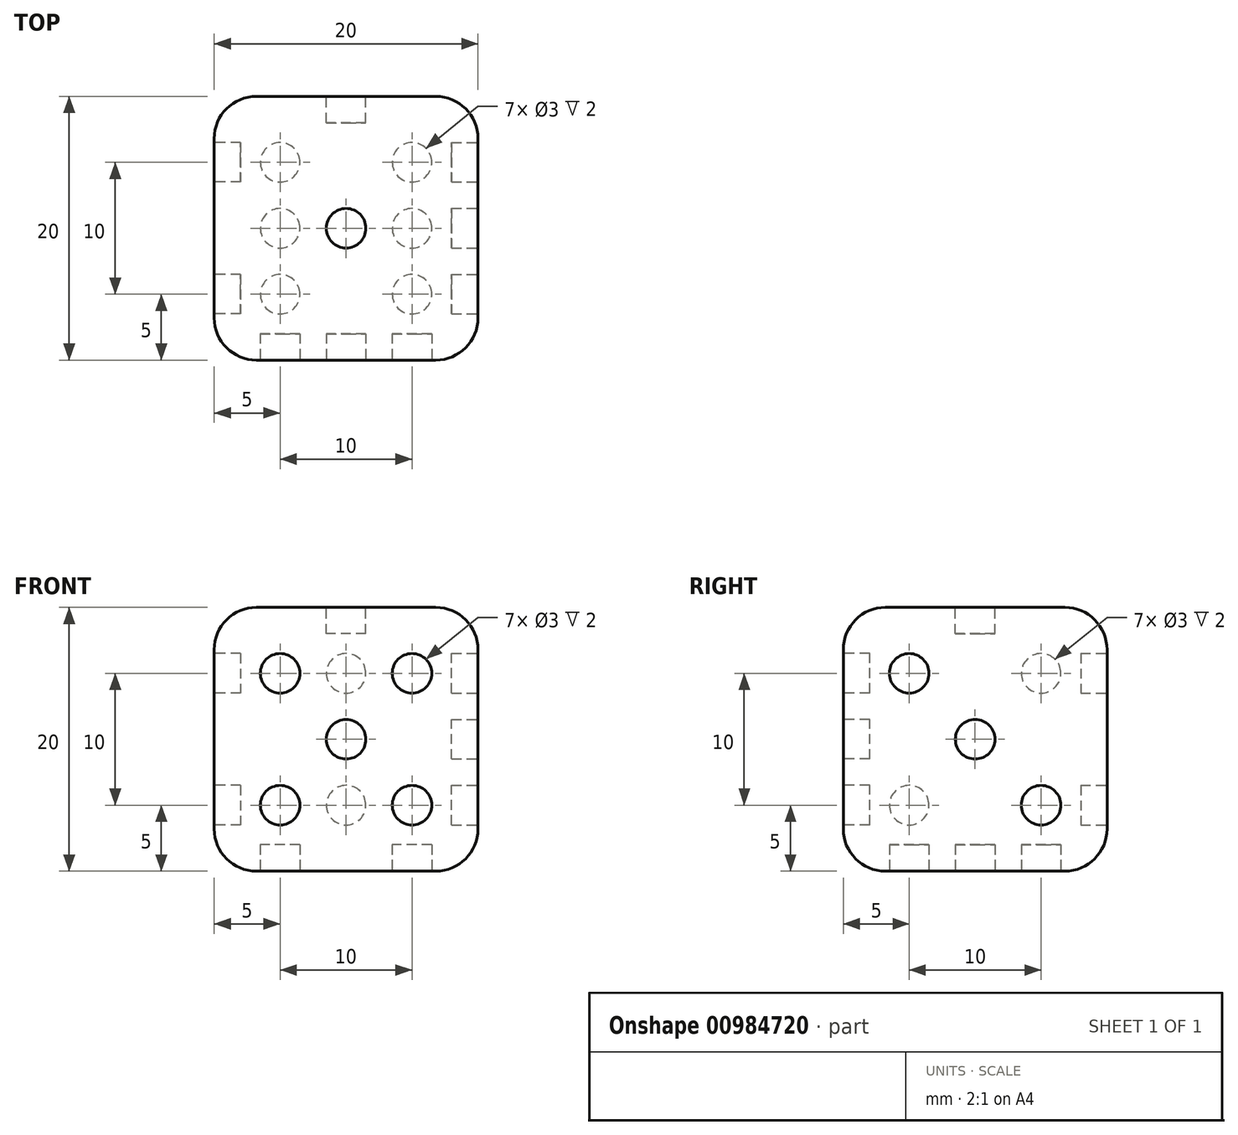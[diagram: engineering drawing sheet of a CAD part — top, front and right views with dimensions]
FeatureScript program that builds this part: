
annotation { "Feature Type Name" : "Feature", "Feature Type Description" : "" }
export const myFeature = defineFeature(function(context is Context, id is Id, definition is map)
    precondition{}
    {
        {
            var Q0;
            Q0=qCreatedBy(makeId("Top.planeOp"),FACE);
            var sketch = newSketch(context, id + "F0", { "sketchPlane" : qUnion([Q0])});
            skLineSegment(sketch, "E0.bottom", {"start": v(-10, -10) * mm, "end": v(10, -10) * mm});
            skLineSegment(sketch, "E0.top", {"start": v(-10, 10) * mm, "end": v(10, 10) * mm});
            skLineSegment(sketch, "E0.left", {"start": v(-10, -10) * mm, "end": v(-10, 10) * mm});
            skLineSegment(sketch, "E0.right", {"start": v(10, -10) * mm, "end": v(10, 10) * mm});
            skSolve(sketch);
        }
        {
            var Q0;
            Q0 = qSketchRegion(id + "F0", true);
            extrude(context, id + "F1", {"entities" : qUnion([Q0]), "depth" : 20 * mm, "offsetDistance" : 25 * mm});
        }
        {
            var Q0;
            Q0=makeQuery(id+"F0.imprint","IMPRINT",FACE,{"disambiguationData":[TD([[makeQuery(id+"F0.imprint","IMPRINT",EDGE,{"derivedFrom":sQuery(id+"F0.wireOp",EDGE,"E0.bottom")}),1.0]])]});
            var sketch = newSketch(context, id + "F2", { "sketchPlane" : qUnion([Q0])});
            skCircle(sketch, "E1", {"center": v(-5, 5) * mm, "radius": 1.5 * mm});
            skCircle(sketch, "E2.1.0.0", {"center": v(5, 5) * mm, "radius": 1.5 * mm});
            skLineSegment(sketch, "E2.direction1", {"start": v(-5, 5) * mm, "end": v(5, 5) * mm, "construction": true});
            skCircle(sketch, "E3.1.0.0", {"center": v(-5, 0) * mm, "radius": 1.5 * mm});
            skCircle(sketch, "E3.1.0.1", {"center": v(5, 0) * mm, "radius": 1.5 * mm});
            skCircle(sketch, "E3.2.0.0", {"center": v(-5, -5) * mm, "radius": 1.5 * mm});
            skCircle(sketch, "E3.2.0.1", {"center": v(5, -5) * mm, "radius": 1.5 * mm});
            skLineSegment(sketch, "E3.direction1", {"start": v(-5, 5) * mm, "end": v(-5, 0) * mm, "construction": true});
            skSolve(sketch);
        }
        {
            var Q0;
            Q0 = qSketchRegion(id + "F2", true);
            extrude(context, id + "F3", {"entities" : qUnion([Q0]), "operationType" : NewBodyOperationType.REMOVE, "depth" : 2 * mm, "offsetDistance" : 25 * mm});
        }
        {
            var Q0;
            Q0=makeQuery(id+"F1.opExtrude","CAP_FACE",FACE,{"disambiguationData":[OSD([sQuery(id+"F0.wireOp",EDGE,"E0.bottom"),sQuery(id+"F0.wireOp",EDGE,"E0.top"),sQuery(id+"F0.wireOp",EDGE,"E0.left"),sQuery(id+"F0.wireOp",EDGE,"E0.right")])],"isStart":false});
            var sketch = newSketch(context, id + "F4", { "sketchPlane" : qUnion([Q0])});
            skCircle(sketch, "E4", {"center": v(0, 0) * mm, "radius": 1.5 * mm});
            skSolve(sketch);
        }
        {
            var Q0;
            Q0 = qSketchRegion(id + "F4", true);
            extrude(context, id + "F5", {"entities" : qUnion([Q0]), "operationType" : NewBodyOperationType.REMOVE, "oppositeDirection" : true, "depth" : 2 * mm, "offsetDistance" : 25 * mm});
        }
        {
            var Q0;
            Q0=makeQuery(id+"F1.opExtrude","SWEPT_FACE",FACE,{"disambiguationData":[OSD([sQuery(id+"F0.wireOp",EDGE,"E0.bottom")])]});
            var sketch = newSketch(context, id + "F6", { "sketchPlane" : qUnion([Q0])});
            skCircle(sketch, "E5", {"center": v(0, 10) * mm, "radius": 1.5 * mm});
            skCircle(sketch, "E6", {"center": v(-5, 5) * mm, "radius": 1.5 * mm});
            skCircle(sketch, "E7.0.1.0", {"center": v(-5, 15) * mm, "radius": 1.5 * mm});
            skCircle(sketch, "E7.1.0.0", {"center": v(5, 5) * mm, "radius": 1.5 * mm});
            skCircle(sketch, "E7.1.1.0", {"center": v(5, 15) * mm, "radius": 1.5 * mm});
            skLineSegment(sketch, "E7.direction1", {"start": v(-5, 5) * mm, "end": v(5, 5) * mm, "construction": true});
            skLineSegment(sketch, "E7.direction2", {"start": v(-5, 5) * mm, "end": v(-5, 15) * mm, "construction": true});
            skSolve(sketch);
        }
        {
            var Q0;
            Q0 = qSketchRegion(id + "F6", true);
            extrude(context, id + "F7", {"entities" : qUnion([Q0]), "operationType" : NewBodyOperationType.REMOVE, "oppositeDirection" : true, "depth" : 2 * mm, "offsetDistance" : 25 * mm});
        }
        {
            var Q0;
            Q0=makeQuery(id+"F1.opExtrude","SWEPT_FACE",FACE,{"disambiguationData":[OSD([sQuery(id+"F0.wireOp",EDGE,"E0.left")])]});
            var sketch = newSketch(context, id + "F8", { "sketchPlane" : qUnion([Q0])});
            skCircle(sketch, "E8", {"center": v(-5, 5) * mm, "radius": 1.5 * mm});
            skCircle(sketch, "E9.0.1.0", {"center": v(-5, 15) * mm, "radius": 1.5 * mm});
            skCircle(sketch, "E9.1.0.0", {"center": v(5, 5) * mm, "radius": 1.5 * mm});
            skCircle(sketch, "E9.1.1.0", {"center": v(5, 15) * mm, "radius": 1.5 * mm});
            skLineSegment(sketch, "E9.direction1", {"start": v(-5, 5) * mm, "end": v(5, 5) * mm, "construction": true});
            skLineSegment(sketch, "E9.direction2", {"start": v(-5, 5) * mm, "end": v(-5, 15) * mm, "construction": true});
            skSolve(sketch);
        }
        {
            var Q0;
            Q0 = qSketchRegion(id + "F8", true);
            extrude(context, id + "F9", {"entities" : qUnion([Q0]), "operationType" : NewBodyOperationType.REMOVE, "oppositeDirection" : true, "depth" : 2 * mm, "offsetDistance" : 25 * mm});
        }
        {
            var Q0;
            Q0=makeQuery(id+"F1.opExtrude","SWEPT_FACE",FACE,{"disambiguationData":[OSD([sQuery(id+"F0.wireOp",EDGE,"E0.right")])]});
            var sketch = newSketch(context, id + "F10", { "sketchPlane" : qUnion([Q0])});
            skCircle(sketch, "E10", {"center": v(-5, 15) * mm, "radius": 1.5 * mm});
            skCircle(sketch, "E11", {"center": v(0, 10) * mm, "radius": 1.5 * mm});
            skCircle(sketch, "E12", {"center": v(5, 5) * mm, "radius": 1.5 * mm});
            skSolve(sketch);
        }
        {
            var Q0;
            Q0=makeQuery(id+"F10.imprint","IMPRINT",FACE,{"disambiguationData":[TD([[makeQuery(id+"F10.imprint","IMPRINT",EDGE,{"derivedFrom":sQuery(id+"F10.wireOp",EDGE,"E12")}),1.0]])]});
            var Q1;
            Q1=makeQuery(id+"F10.imprint","IMPRINT",FACE,{"disambiguationData":[TD([[makeQuery(id+"F10.imprint","IMPRINT",EDGE,{"derivedFrom":sQuery(id+"F10.wireOp",EDGE,"E11")}),1.0]])]});
            var Q2;
            Q2=makeQuery(id+"F10.imprint","IMPRINT",FACE,{"disambiguationData":[TD([[makeQuery(id+"F10.imprint","IMPRINT",EDGE,{"derivedFrom":sQuery(id+"F10.wireOp",EDGE,"E10")}),1.0]])]});
            extrude(context, id + "F11", {"entities" : qUnion([Q0, Q1, Q2]), "operationType" : NewBodyOperationType.REMOVE, "oppositeDirection" : true, "depth" : 2 * mm, "offsetDistance" : 25 * mm});
        }
        {
            var Q0;
            Q0=makeQuery(id+"F1.opExtrude","SWEPT_FACE",FACE,{"disambiguationData":[OSD([sQuery(id+"F0.wireOp",EDGE,"E0.top")])]});
            var sketch = newSketch(context, id + "F12", { "sketchPlane" : qUnion([Q0])});
            skCircle(sketch, "E13", {"center": v(0, 5) * mm, "radius": 1.5 * mm});
            skCircle(sketch, "E14", {"center": v(0, 15) * mm, "radius": 1.5 * mm});
            skSolve(sketch);
        }
        {
            var Q0;
            Q0=makeQuery(id+"F12.imprint","IMPRINT",FACE,{"disambiguationData":[TD([[makeQuery(id+"F12.imprint","IMPRINT",EDGE,{"derivedFrom":sQuery(id+"F12.wireOp",EDGE,"E13")}),1.0]])]});
            var Q1;
            Q1=makeQuery(id+"F12.imprint","IMPRINT",FACE,{"disambiguationData":[TD([[makeQuery(id+"F12.imprint","IMPRINT",EDGE,{"derivedFrom":sQuery(id+"F12.wireOp",EDGE,"E14")}),1.0]])]});
            extrude(context, id + "F13", {"entities" : qUnion([Q0, Q1]), "operationType" : NewBodyOperationType.REMOVE, "oppositeDirection" : true, "depth" : 2 * mm, "offsetDistance" : 25 * mm});
        }
        {
            var Q0;
            Q0=makeQuery(id+"F1.opExtrude","CAP_EDGE",EDGE,{"disambiguationData":[OSD([sQuery(id+"F0.wireOp",EDGE,"E0.right")])],"isStart":false});
            var Q1;
            Q1=makeQuery(id+"F1.opExtrude","SWEPT_EDGE",EDGE,{"disambiguationData":[OSD([sQuery(id+"F0.wireOp",EDGE,"E0.top"),sQuery(id+"F0.wireOp",EDGE,"E0.right")])]});
            var Q2;
            Q2=makeQuery(id+"F1.opExtrude","CAP_EDGE",EDGE,{"disambiguationData":[OSD([sQuery(id+"F0.wireOp",EDGE,"E0.top")])],"isStart":false});
            var Q3;
            Q3=makeQuery(id+"F1.opExtrude","SWEPT_EDGE",EDGE,{"disambiguationData":[OSD([sQuery(id+"F0.wireOp",EDGE,"E0.bottom"),sQuery(id+"F0.wireOp",EDGE,"E0.right")])]});
            var Q4;
            Q4=makeQuery(id+"F1.opExtrude","CAP_EDGE",EDGE,{"disambiguationData":[OSD([sQuery(id+"F0.wireOp",EDGE,"E0.right")])],"isStart":true});
            var Q5;
            Q5=makeQuery(id+"F1.opExtrude","CAP_EDGE",EDGE,{"disambiguationData":[OSD([sQuery(id+"F0.wireOp",EDGE,"E0.top")])],"isStart":true});
            var Q6;
            Q6=makeQuery(id+"F1.opExtrude","CAP_EDGE",EDGE,{"disambiguationData":[OSD([sQuery(id+"F0.wireOp",EDGE,"E0.bottom")])],"isStart":false});
            var Q7;
            Q7=makeQuery(id+"F1.opExtrude","CAP_EDGE",EDGE,{"disambiguationData":[OSD([sQuery(id+"F0.wireOp",EDGE,"E0.left")])],"isStart":false});
            var Q8;
            Q8=makeQuery(id+"F1.opExtrude","CAP_EDGE",EDGE,{"disambiguationData":[OSD([sQuery(id+"F0.wireOp",EDGE,"E0.bottom")])],"isStart":true});
            var Q9;
            Q9=makeQuery(id+"F1.opExtrude","CAP_EDGE",EDGE,{"disambiguationData":[OSD([sQuery(id+"F0.wireOp",EDGE,"E0.left")])],"isStart":true});
            var Q10;
            Q10=makeQuery(id+"F1.opExtrude","SWEPT_EDGE",EDGE,{"disambiguationData":[OSD([sQuery(id+"F0.wireOp",EDGE,"E0.bottom"),sQuery(id+"F0.wireOp",EDGE,"E0.left")])]});
            var Q11;
            Q11=makeQuery(id+"F1.opExtrude","SWEPT_EDGE",EDGE,{"disambiguationData":[OSD([sQuery(id+"F0.wireOp",EDGE,"E0.top"),sQuery(id+"F0.wireOp",EDGE,"E0.left")])]});
            fillet(context, id + "F14", {"entities" : qUnion([Q0, Q1, Q2, Q3, Q4, Q5, Q6, Q7, Q8, Q9, Q10, Q11]), "radius" : 3.2 * mm, "tangentPropagation" : true, "defaultsChanged" : true, "vertexSettings" : [], "allowEdgeOverflow" : false});
        }
    });
